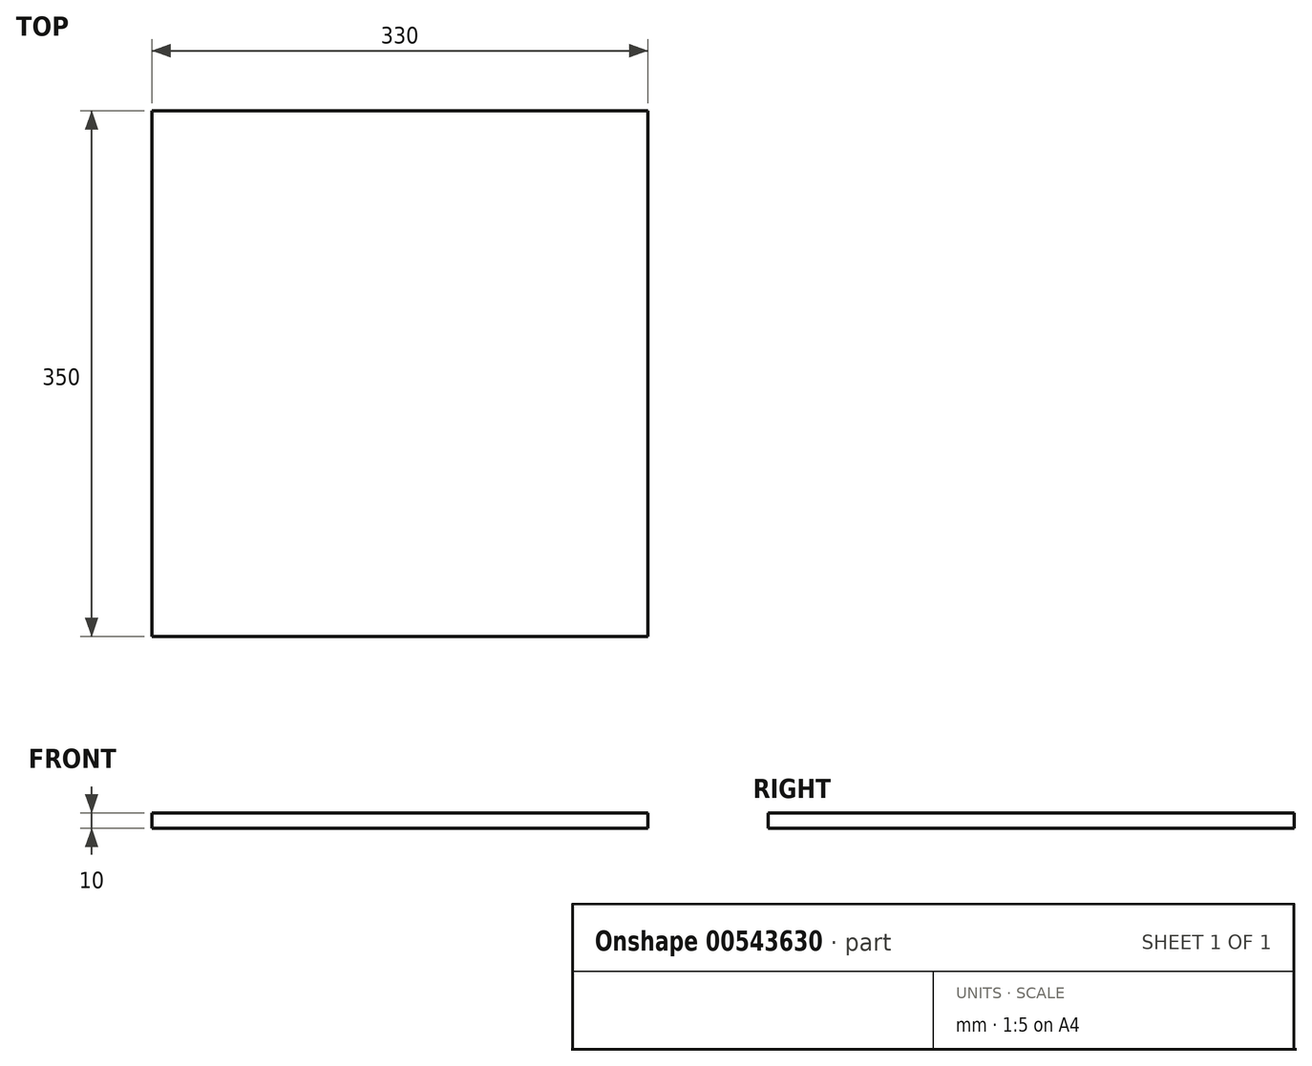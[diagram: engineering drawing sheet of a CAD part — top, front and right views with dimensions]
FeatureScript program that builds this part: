
annotation { "Feature Type Name" : "Feature", "Feature Type Description" : "" }
export const myFeature = defineFeature(function(context is Context, id is Id, definition is map)
    precondition{}
    {
        {
            var Q0;
            Q0=qCreatedBy(makeId("Top.planeOp"),FACE);
            var sketch = newSketch(context, id + "F0", { "sketchPlane" : qUnion([Q0])});
            skLineSegment(sketch, "E0.bottom", {"start": v(-70.96, 65.05) * mm, "end": v(259.04, 65.05) * mm});
            skLineSegment(sketch, "E0.top", {"start": v(-70.96, -284.95) * mm, "end": v(259.04, -284.95) * mm});
            skLineSegment(sketch, "E0.left", {"start": v(-70.96, 65.05) * mm, "end": v(-70.96, -284.95) * mm});
            skLineSegment(sketch, "E0.right", {"start": v(259.04, 65.05) * mm, "end": v(259.04, -284.95) * mm});
            skSolve(sketch);
        }
        {
            var Q0;
            Q0=qSketchRegion(id+"F0",true);
            extrude(context, id + "F1", {"entities" : qUnion([Q0]), "depth" : 10 * mm});
        }
        {
            var Q0;
            Q0=makeQuery(id+"F1.opExtrude","CAP_FACE",FACE,{"disambiguationData":[OSD([sQuery(id+"F0.wireOp",EDGE,"E0.bottom"),sQuery(id+"F0.wireOp",EDGE,"E0.top"),sQuery(id+"F0.wireOp",EDGE,"E0.left"),sQuery(id+"F0.wireOp",EDGE,"E0.right")])],"isStart":true});
            extrude(context, id + "F2", {"entities" : qUnion([Q0]), "operationType" : NewBodyOperationType.ADD, "depth" : 2 * mm, "offsetDistance" : 25 * mm});
        }
        {
            var Q0;
            Q0=makeQuery(id+"F2.opExtrude","CAP_FACE",FACE,{"disambiguationData":[OSD([sQuery(id+"F0.wireOp",EDGE,"E0.bottom"),sQuery(id+"F0.wireOp",EDGE,"E0.top"),sQuery(id+"F0.wireOp",EDGE,"E0.left"),sQuery(id+"F0.wireOp",EDGE,"E0.right")])],"isStart":false});
            extrude(context, id + "F3", {"entities" : qUnion([Q0]), "operationType" : NewBodyOperationType.REMOVE, "oppositeDirection" : true, "depth" : 2 * mm, "offsetDistance" : 25 * mm});
        }
    });
